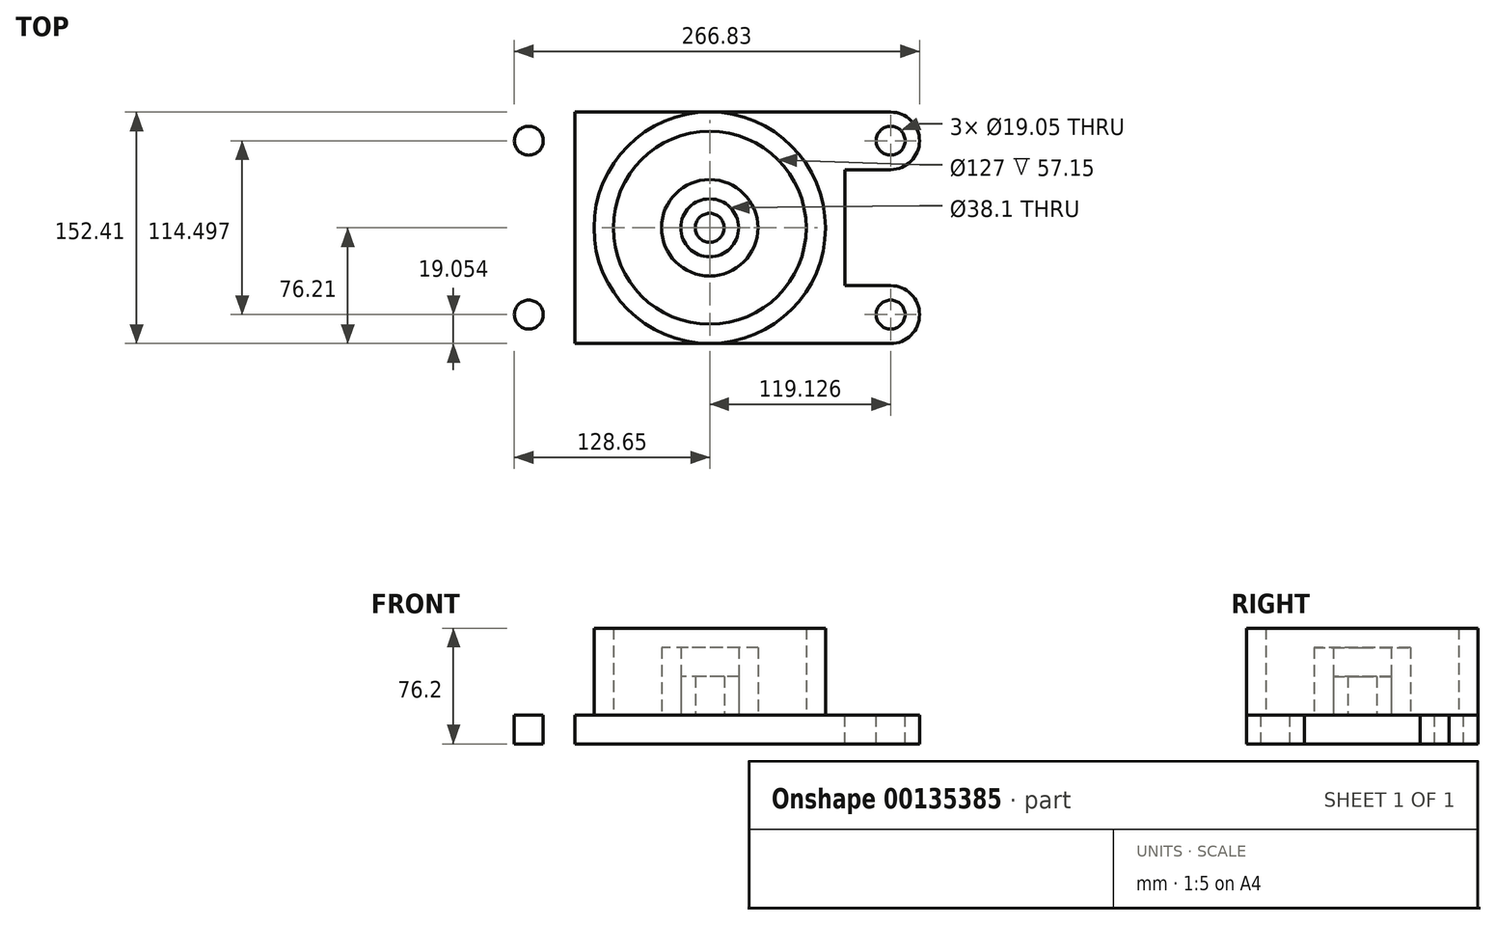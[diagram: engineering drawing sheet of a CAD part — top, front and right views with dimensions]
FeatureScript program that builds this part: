
annotation { "Feature Type Name" : "Feature", "Feature Type Description" : "" }
export const myFeature = defineFeature(function(context is Context, id is Id, definition is map)
    precondition{}
    {
        {
            var Q0;
            Q0=qCreatedBy(makeId("Top.planeOp"),FACE);
            var sketch = newSketch(context, id + "F0", { "sketchPlane" : qUnion([Q0])});
            skCircle(sketch, "E0", {"center": v(0, 0) * mm, "radius": 19.05 * mm});
            skCircle(sketch, "E1", {"center": v(0, 0) * mm, "radius": 63.5 * mm});
            skCircle(sketch, "E2", {"center": v(0, 0) * mm, "radius": 76.2 * mm});
            skCircle(sketch, "E3", {"center": v(0, 0) * mm, "radius": 31.75 * mm});
            skLineSegment(sketch, "E4", {"start": v(-88.9, 76.2) * mm, "end": v(76.2, 76.2) * mm});
            skLineSegment(sketch, "E5", {"start": v(76.2, 76.2) * mm, "end": v(88.9, 76.2) * mm});
            skLineSegment(sketch, "E6", {"start": v(88.9, 76.2) * mm, "end": v(-88.9, 76.2) * mm});
            skLineSegment(sketch, "E7", {"start": v(88.9, 76.2) * mm, "end": v(88.9, -76.2) * mm});
            skLineSegment(sketch, "E8", {"start": v(-88.9, 76.2) * mm, "end": v(-88.9, -76.2) * mm});
            skLineSegment(sketch, "E9", {"start": v(-88.9, -76.2) * mm, "end": v(88.9, -76.2) * mm});
            skPoint(sketch, "E10.start.orphan", {"position": v(76.33, -76.2) * mm});
            skLineSegment(sketch, "E11", {"start": v(88.9, 76.2) * mm, "end": v(119.13, 76.2) * mm});
            skLineSegment(sketch, "E12", {"start": v(138.18, 57.34) * mm, "end": v(138.18, 57.15) * mm});
            skLineSegment(sketch, "E13", {"start": v(119.13, 38.3) * mm, "end": v(88.9, 38.3) * mm});
            skPoint(sketch, "E14.visualSharp", {"position": v(138.18, 76.2) * mm});
            skArc(sketch, "E14.filletArc", {"start": v(138.18, 57.15) * mm, "mid": v(132.6, 70.62) * mm, "end": v(119.13, 76.2) * mm});
            skPoint(sketch, "E15.visualSharp", {"position": v(138.18, 38.3) * mm});
            skArc(sketch, "E15.filletArc", {"start": v(119.13, 38.3) * mm, "mid": v(132.6, 43.87) * mm, "end": v(138.18, 57.34) * mm});
            skCircle(sketch, "E16", {"center": v(119.13, 57.34) * mm, "radius": 9.53 * mm});
            skLineSegment(sketch, "E17", {"start": v(88.9, -76.2) * mm, "end": v(119.13, -76.2) * mm});
            skLineSegment(sketch, "E18", {"start": v(88.9, 76.2) * mm, "end": v(88.9, 38.3) * mm});
            skLineSegment(sketch, "E19", {"start": v(88.9, -76.2) * mm, "end": v(88.9, -38.1) * mm});
            skLineSegment(sketch, "E20", {"start": v(88.9, -38.1) * mm, "end": v(119.13, -38.1) * mm});
            skArc(sketch, "E21", {"start": v(119.13, -76.2) * mm, "mid": v(138.18, -57.16) * mm, "end": v(119.13, -38.1) * mm});
            skCircle(sketch, "E22", {"center": v(119.13, -57.16) * mm, "radius": 9.53 * mm});
            skLineSegment(sketch, "E23", {"start": v(0, 0) * mm, "end": v(0, 91.88) * mm});
            skLineSegment(sketch, "E24.MirrorCS", {"start": v(-138.18, 57.34) * mm, "end": v(-138.18, 57.15) * mm});
            skPoint(sketch, "E25.MirrorP", {"position": v(-138.18, 76.2) * mm});
            skPoint(sketch, "E26.MirrorP", {"position": v(-138.18, 38.3) * mm});
            skCircle(sketch, "E27.MirrorC", {"center": v(-119.13, 57.34) * mm, "radius": 9.53 * mm});
            skArc(sketch, "E28.MirrorCS", {"start": v(-138.18, 57.15) * mm, "mid": v(-132.6, 70.62) * mm, "end": v(-119.13, 76.2) * mm});
            skArc(sketch, "E29.MirrorCS", {"start": v(-119.13, 38.3) * mm, "mid": v(-132.6, 43.87) * mm, "end": v(-138.18, 57.34) * mm});
            skLineSegment(sketch, "E30.MirrorCS", {"start": v(-88.9, 76.2) * mm, "end": v(-119.13, 76.2) * mm});
            skLineSegment(sketch, "E31.MirrorCS", {"start": v(-119.13, 38.3) * mm, "end": v(-88.9, 38.3) * mm});
            skCircle(sketch, "E32.MirrorC", {"center": v(-119.13, -57.16) * mm, "radius": 9.53 * mm});
            skLineSegment(sketch, "E33.MirrorCS", {"start": v(-88.9, -76.2) * mm, "end": v(-119.13, -76.2) * mm});
            skLineSegment(sketch, "E34.MirrorCS", {"start": v(-88.9, -38.1) * mm, "end": v(-119.13, -38.1) * mm});
            skArc(sketch, "E35.MirrorCS", {"start": v(-119.13, -76.2) * mm, "mid": v(-138.18, -57.16) * mm, "end": v(-119.13, -38.1) * mm});
            skLineSegment(sketch, "E36", {"start": v(-88.9, 76.2) * mm, "end": v(-88.9, 38.3) * mm});
            skLineSegment(sketch, "E37", {"start": v(-88.9, -38.1) * mm, "end": v(-88.9, -76.2) * mm});
            skLineSegment(sketch, "E38", {"start": v(-88.9, 38.3) * mm, "end": v(-88.9, 76.2) * mm});
            skCircle(sketch, "E39", {"center": v(0, 0) * mm, "radius": 9.53 * mm});
            skSolve(sketch);
        }
        {
            var Q0;
            Q0=makeQuery(id+"F0.imprint","IMPRINT",FACE,{"disambiguationData":[TD([[makeQuery(id+"F0.imprint","IMPRINT",EDGE,{"derivedFrom":sQuery(id+"F0.wireOp",EDGE,"E27.MirrorC")}),1.0]])]});
            var Q1;
            Q1=makeQuery(id+"F0.imprint","IMPRINT",FACE,{"disambiguationData":[TD([[makeQuery(id+"F0.imprint","IMPRINT",EDGE,{"derivedFrom":sQuery(id+"F0.wireOp",EDGE,"E32.MirrorC")}),1.0]])]});
            var Q2;
            {var subQ4=sQuery(id+"F0.wireOp",EDGE,"E11");Q2=makeQuery(id+"F0.imprint","IMPRINT",FACE,{"disambiguationData":[TD([[makeQuery(id+"F0.imprint","IMPRINT",EDGE,{"derivedFrom":subQ4}),-1.0]])]});}
            var Q3;
            Q3=makeQuery(id+"F0.imprint","IMPRINT",FACE,{"disambiguationData":[TD([[makeQuery(id+"F0.imprint","IMPRINT",EDGE,{"derivedFrom":sQuery(id+"F0.wireOp",EDGE,"E17")}),1.0]])]});
            var Q4;
            {var subQ2=sQuery(id+"F0.wireOp",EDGE,"E2");Q4=makeQuery(id+"F0.imprint","IMPRINT",FACE,{"disambiguationData":[TD([[makeQuery(id+"F0.imprint","IMPRINT",EDGE,{"derivedFrom":subQ2}),-1.0]])]});}
            var Q5;
            Q5=makeQuery(id+"F0.imprint","IMPRINT",FACE,{"disambiguationData":[TD([[makeQuery(id+"F0.imprint","IMPRINT",EDGE,{"derivedFrom":sQuery(id+"F0.wireOp",EDGE,"E1")}),-1.0]])]});
            var Q6;
            Q6=makeQuery(id+"F0.imprint","IMPRINT",FACE,{"disambiguationData":[TD([[makeQuery(id+"F0.imprint","IMPRINT",EDGE,{"derivedFrom":sQuery(id+"F0.wireOp",EDGE,"E1")}),1.0]])]});
            var Q7;
            Q7=makeQuery(id+"F0.imprint","IMPRINT",FACE,{"disambiguationData":[TD([[makeQuery(id+"F0.imprint","IMPRINT",EDGE,{"derivedFrom":sQuery(id+"F0.wireOp",EDGE,"E0")}),-1.0]])]});
            var Q8;
            Q8=makeQuery(id+"F0.imprint","IMPRINT",FACE,{"disambiguationData":[TD([[makeQuery(id+"F0.imprint","IMPRINT",EDGE,{"derivedFrom":sQuery(id+"F0.wireOp",EDGE,"E0")}),1.0]])]});
            var Q9;
            Q9=makeQuery(id+"F0.imprint","IMPRINT",FACE,{"disambiguationData":[TD([[makeQuery(id+"F0.imprint","IMPRINT",EDGE,{"derivedFrom":sQuery(id+"F0.wireOp",EDGE,"E39")}),1.0]])]});
            extrude(context, id + "F1", {"entities" : qUnion([Q0, Q1, Q2, Q3, Q4, Q5, Q6, Q7, Q8, Q9]), "oppositeDirection" : true, "depth" : 19.05 * mm});
        }
        {
            var Q0;
            Q0=makeQuery(id+"F0.imprint","IMPRINT",FACE,{"disambiguationData":[TD([[makeQuery(id+"F0.imprint","IMPRINT",EDGE,{"derivedFrom":sQuery(id+"F0.wireOp",EDGE,"E1")}),-1.0]])]});
            extrude(context, id + "F2", {"entities" : qUnion([Q0]), "depth" : 57.15 * mm});
        }
        {
            var Q0;
            Q0=makeQuery(id+"F0.imprint","IMPRINT",FACE,{"disambiguationData":[TD([[makeQuery(id+"F0.imprint","IMPRINT",EDGE,{"derivedFrom":sQuery(id+"F0.wireOp",EDGE,"E0")}),-1.0]])]});
            extrude(context, id + "F3", {"entities" : qUnion([Q0]), "depth" : 44.45 * mm});
        }
        {
            var Q0;
            Q0=makeQuery(id+"F0.imprint","IMPRINT",FACE,{"disambiguationData":[TD([[makeQuery(id+"F0.imprint","IMPRINT",EDGE,{"derivedFrom":sQuery(id+"F0.wireOp",EDGE,"E0")}),1.0]])]});
            extrude(context, id + "F4", {"entities" : qUnion([Q0]), "depth" : 25.4 * mm});
        }
    });
